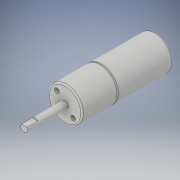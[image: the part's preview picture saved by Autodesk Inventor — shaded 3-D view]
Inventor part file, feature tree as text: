
AUTODESK INVENTOR PART (.ipt)
format: ipt  version: 2019 (Build 230136000, 136)  size: 145,408 bytes
history: native  units: mm
features: extrude x5, sketch x5, fillet x2, projected_geometry x1
ambient origin geometry x8: Origin, YZ Plane, XZ Plane, XY Plane, X Axis, Y Axis, Z Axis, Center Point
bodies: Solid1 (feature_tree)
feature tree (13):
  extrude  "Extrusion1"  Depth=26.5mm TaperAngle=0.0deg
  fillet  "Fillet1"  Radius=1.0mm
  extrude  "Extrusion2"  Depth=3.5mm
  extrude  "Extrusion3"  Depth=10.0mm TaperAngle=0.0deg
  extrude  "Extrusion4"  Depth=40.0mm TaperAngle=0.0deg
  extrude  "Extrusion5"  Depth=30.0mm TaperAngle=0.0deg
  fillet  "Fillet2"  Radius=8.0mm
  sketch  "Sketch1"  dims[d0=25.0mm d1=26.5mm d2=0.0mm d3=1.0mm]
  sketch  "Sketch2"  dims[d5=3.5mm d6=3.5mm]
  sketch  "Sketch3"  dims[d7=16.5mm d8=10.0mm d9=0.0mm]
  sketch  "Sketch4"  dims[d10=24.9mm d11=40.0mm d12=0.0mm]
  sketch  "Sketch5"  dims[d13=5.0mm d14=30.0mm d15=0.0mm d16=8.0mm d17=0.0mm d18=1.0mm]
  projected_geometry  "Projected Loop1"
